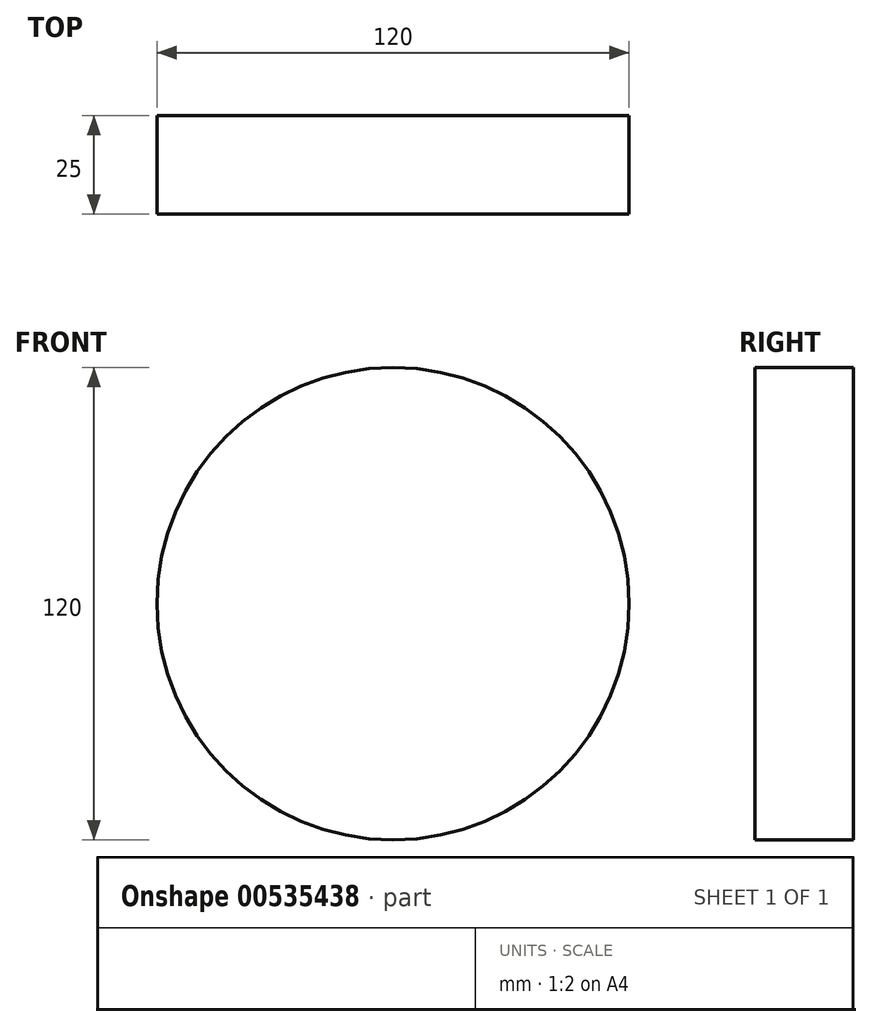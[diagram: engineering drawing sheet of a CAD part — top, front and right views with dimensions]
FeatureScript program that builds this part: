
annotation { "Feature Type Name" : "Feature", "Feature Type Description" : "" }
export const myFeature = defineFeature(function(context is Context, id is Id, definition is map)
    precondition{}
    {
        {
            var Q0;
            Q0=qCreatedBy(makeId("Front.planeOp"),FACE);
            var sketch = newSketch(context, id + "F0", { "sketchPlane" : qUnion([Q0])});
            skCircle(sketch, "E0", {"center": v(0, 0) * mm, "radius": 60 * mm});
            skSolve(sketch);
        }
        {
            var Q0;
            Q0 = qSketchRegion(id + "F0", true);
            extrude(context, id + "F1", {"entities" : qUnion([Q0]), "depth" : 25 * mm, "offsetDistance" : 25 * mm});
        }
    });
